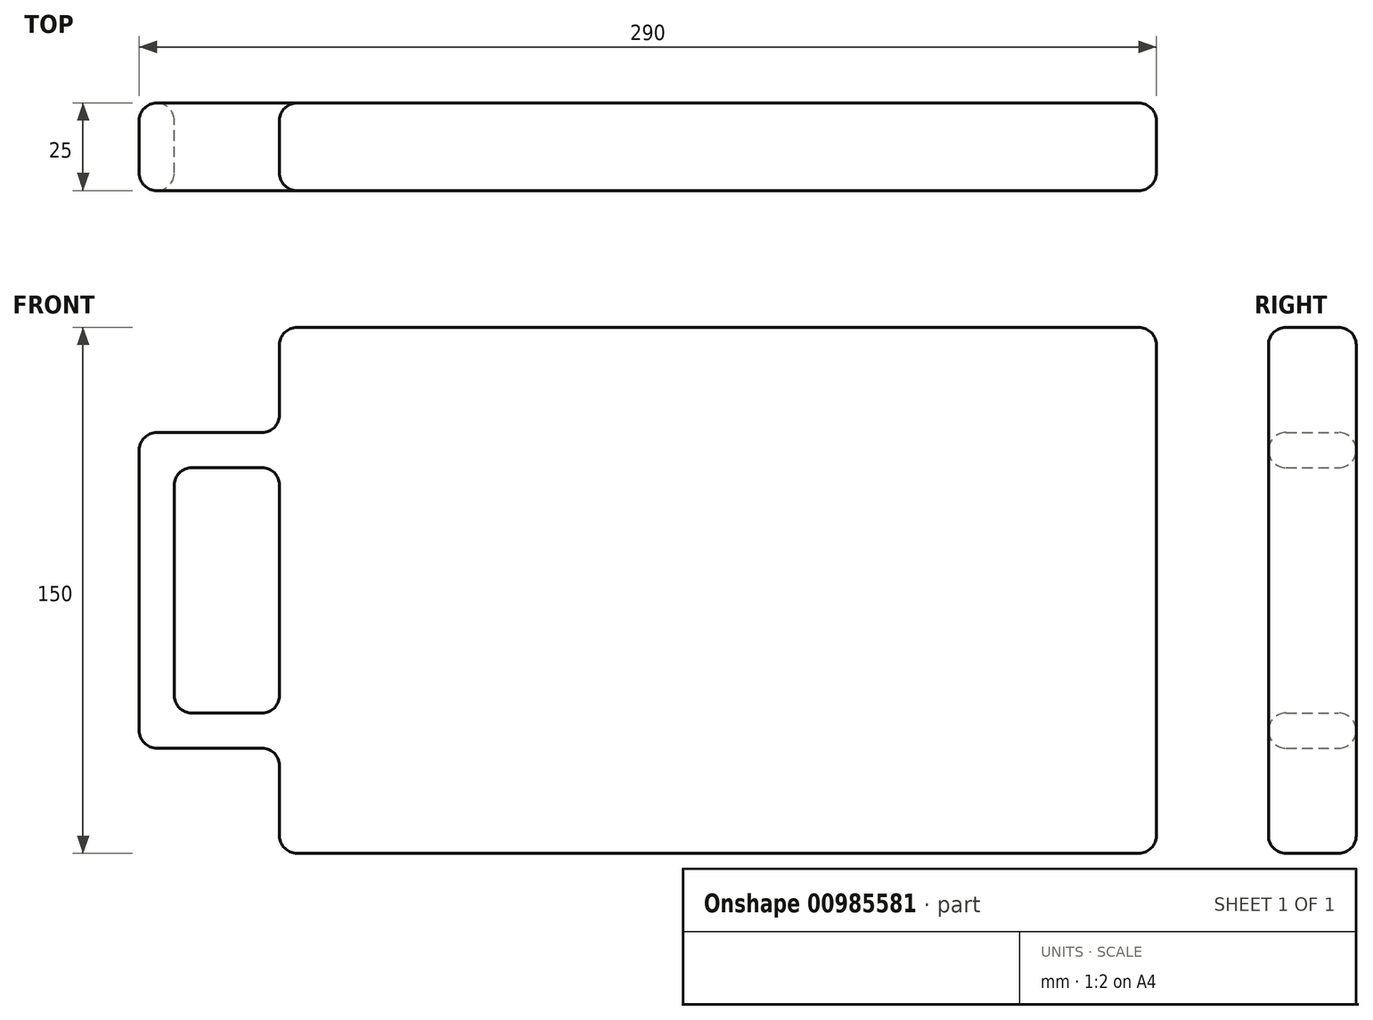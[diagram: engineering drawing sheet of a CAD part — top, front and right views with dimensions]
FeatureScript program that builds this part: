
annotation { "Feature Type Name" : "Feature", "Feature Type Description" : "" }
export const myFeature = defineFeature(function(context is Context, id is Id, definition is map)
    precondition{}
    {
        {
            var Q0;
            Q0=qCreatedBy(makeId("Front.planeOp"),FACE);
            var sketch = newSketch(context, id + "F0", { "sketchPlane" : qUnion([Q0])});
            skLineSegment(sketch, "E0.bottom", {"start": v(125, 75) * mm, "end": v(-125, 75) * mm});
            skLineSegment(sketch, "E0.top", {"start": v(125, -75) * mm, "end": v(-125, -75) * mm});
            skLineSegment(sketch, "E0.left", {"start": v(125, 75) * mm, "end": v(125, -75) * mm});
            skLineSegment(sketch, "E0.right", {"start": v(-125, 75) * mm, "end": v(-125, -75) * mm});
            skLineSegment(sketch, "E1.bottom", {"start": v(-125, -45) * mm, "end": v(-165, -45) * mm});
            skLineSegment(sketch, "E1.top", {"start": v(-125, 45) * mm, "end": v(-165, 45) * mm});
            skLineSegment(sketch, "E1.left", {"start": v(-125, -45) * mm, "end": v(-125, 45) * mm});
            skLineSegment(sketch, "E1.right", {"start": v(-165, -45) * mm, "end": v(-165, 45) * mm});
            skLineSegment(sketch, "E2.bottom", {"start": v(-125, 35) * mm, "end": v(-155, 35) * mm});
            skLineSegment(sketch, "E2.top", {"start": v(-125, -35) * mm, "end": v(-155, -35) * mm});
            skLineSegment(sketch, "E2.left", {"start": v(-125, 35) * mm, "end": v(-125, -35) * mm});
            skLineSegment(sketch, "E2.right", {"start": v(-155, 35) * mm, "end": v(-155, -35) * mm});
            skSolve(sketch);
        }
        {
            var Q0;
            {var subQ5=sQuery(id+"F0.wireOp",EDGE,"E1.bottom");Q0=makeQuery(id+"F0.imprint","IMPRINT",FACE,{"disambiguationData":[TD([[makeQuery(id+"F0.imprint","IMPRINT",EDGE,{"derivedFrom":subQ5}),-1.0]])]});}
            var Q1;
            {var subQ1=sQuery(id+"F0.wireOp",EDGE,"E0.bottom");Q1=makeQuery(id+"F0.imprint","IMPRINT",FACE,{"disambiguationData":[TD([[makeQuery(id+"F0.imprint","IMPRINT",EDGE,{"derivedFrom":subQ1}),1.0]])]});}
            extrude(context, id + "F1", {"entities" : qUnion([Q0, Q1]), "depth" : 25 * mm, "offsetDistance" : 25 * mm});
        }
        {
            var Q0;
            Q0=makeQuery(id+"F1.opExtrude","SWEPT_EDGE",EDGE,{"disambiguationData":[OSD([sQuery(id+"F0.wireOp",EDGE,"E0.right"),sQuery(id+"F0.wireOp",EDGE,"E1.top"),sQuery(id+"F0.wireOp",EDGE,"E1.left")])]});
            var Q1;
            Q1=makeQuery(id+"F1.opExtrude","SWEPT_EDGE",EDGE,{"disambiguationData":[OSD([sQuery(id+"F0.wireOp",EDGE,"E1.top"),sQuery(id+"F0.wireOp",EDGE,"E1.right")])]});
            var Q2;
            Q2=makeQuery(id+"F1.opExtrude","SWEPT_EDGE",EDGE,{"disambiguationData":[OSD([sQuery(id+"F0.wireOp",EDGE,"E1.bottom"),sQuery(id+"F0.wireOp",EDGE,"E1.right")])]});
            var Q3;
            Q3=makeQuery(id+"F1.opExtrude","SWEPT_EDGE",EDGE,{"disambiguationData":[OSD([sQuery(id+"F0.wireOp",EDGE,"E0.right"),sQuery(id+"F0.wireOp",EDGE,"E1.bottom"),sQuery(id+"F0.wireOp",EDGE,"E1.left")])]});
            var Q4;
            Q4=makeQuery(id+"F1.opExtrude","SWEPT_EDGE",EDGE,{"disambiguationData":[OSD([sQuery(id+"F0.wireOp",EDGE,"E1.left"),sQuery(id+"F0.wireOp",EDGE,"E2.top"),sQuery(id+"F0.wireOp",EDGE,"E2.left")])]});
            var Q5;
            Q5=makeQuery(id+"F1.opExtrude","SWEPT_EDGE",EDGE,{"disambiguationData":[OSD([sQuery(id+"F0.wireOp",EDGE,"E2.top"),sQuery(id+"F0.wireOp",EDGE,"E2.right")])]});
            var Q6;
            Q6=makeQuery(id+"F1.opExtrude","SWEPT_EDGE",EDGE,{"disambiguationData":[OSD([sQuery(id+"F0.wireOp",EDGE,"E2.bottom"),sQuery(id+"F0.wireOp",EDGE,"E2.right")])]});
            var Q7;
            Q7=makeQuery(id+"F1.opExtrude","SWEPT_EDGE",EDGE,{"disambiguationData":[OSD([sQuery(id+"F0.wireOp",EDGE,"E1.left"),sQuery(id+"F0.wireOp",EDGE,"E2.bottom"),sQuery(id+"F0.wireOp",EDGE,"E2.left")])]});
            var Q8;
            Q8=makeQuery(id+"F1.opExtrude","SWEPT_EDGE",EDGE,{"disambiguationData":[OSD([sQuery(id+"F0.wireOp",EDGE,"E0.bottom"),sQuery(id+"F0.wireOp",EDGE,"E0.right")])]});
            var Q9;
            Q9=makeQuery(id+"F1.opExtrude","SWEPT_EDGE",EDGE,{"disambiguationData":[OSD([sQuery(id+"F0.wireOp",EDGE,"E0.top"),sQuery(id+"F0.wireOp",EDGE,"E0.right")])]});
            var Q10;
            Q10=makeQuery(id+"F1.opExtrude","SWEPT_EDGE",EDGE,{"disambiguationData":[OSD([sQuery(id+"F0.wireOp",EDGE,"E0.top"),sQuery(id+"F0.wireOp",EDGE,"E0.left")])]});
            var Q11;
            Q11=makeQuery(id+"F1.opExtrude","SWEPT_EDGE",EDGE,{"disambiguationData":[OSD([sQuery(id+"F0.wireOp",EDGE,"E0.bottom"),sQuery(id+"F0.wireOp",EDGE,"E0.left")])]});
            fillet(context, id + "F2", {"entities" : qUnion([Q0, Q1, Q2, Q3, Q4, Q5, Q6, Q7, Q8, Q9, Q10, Q11]), "radius" : 5 * mm, "tangentPropagation" : true, "allowEdgeOverflow" : false});
        }
        {
            var Q0;
            Q0=makeQuery(id+"F1.opExtrude","CAP_EDGE",EDGE,{"disambiguationData":[OSD([sQuery(id+"F0.wireOp",EDGE,"E1.top")])],"isStart":false});
            fillet(context, id + "F3", {"entities" : qUnion([Q0]), "radius" : 5 * mm, "tangentPropagation" : true, "allowEdgeOverflow" : false});
        }
        {
            var Q0;
            Q0=makeQuery(id+"F1.opExtrude","CAP_EDGE",EDGE,{"disambiguationData":[OSD([sQuery(id+"F0.wireOp",EDGE,"E2.bottom")])],"isStart":false});
            var Q1;
            Q1=makeQuery(id+"F1.opExtrude","CAP_EDGE",EDGE,{"disambiguationData":[OSD([sQuery(id+"F0.wireOp",EDGE,"E1.bottom")])],"isStart":true});
            var Q2;
            Q2=makeQuery(id+"F1.opExtrude","CAP_EDGE",EDGE,{"disambiguationData":[OSD([sQuery(id+"F0.wireOp",EDGE,"E2.top")])],"isStart":true});
            fillet(context, id + "F4", {"entities" : qUnion([Q0, Q1, Q2]), "radius" : 5 * mm, "tangentPropagation" : true, "allowEdgeOverflow" : false});
        }
    });
